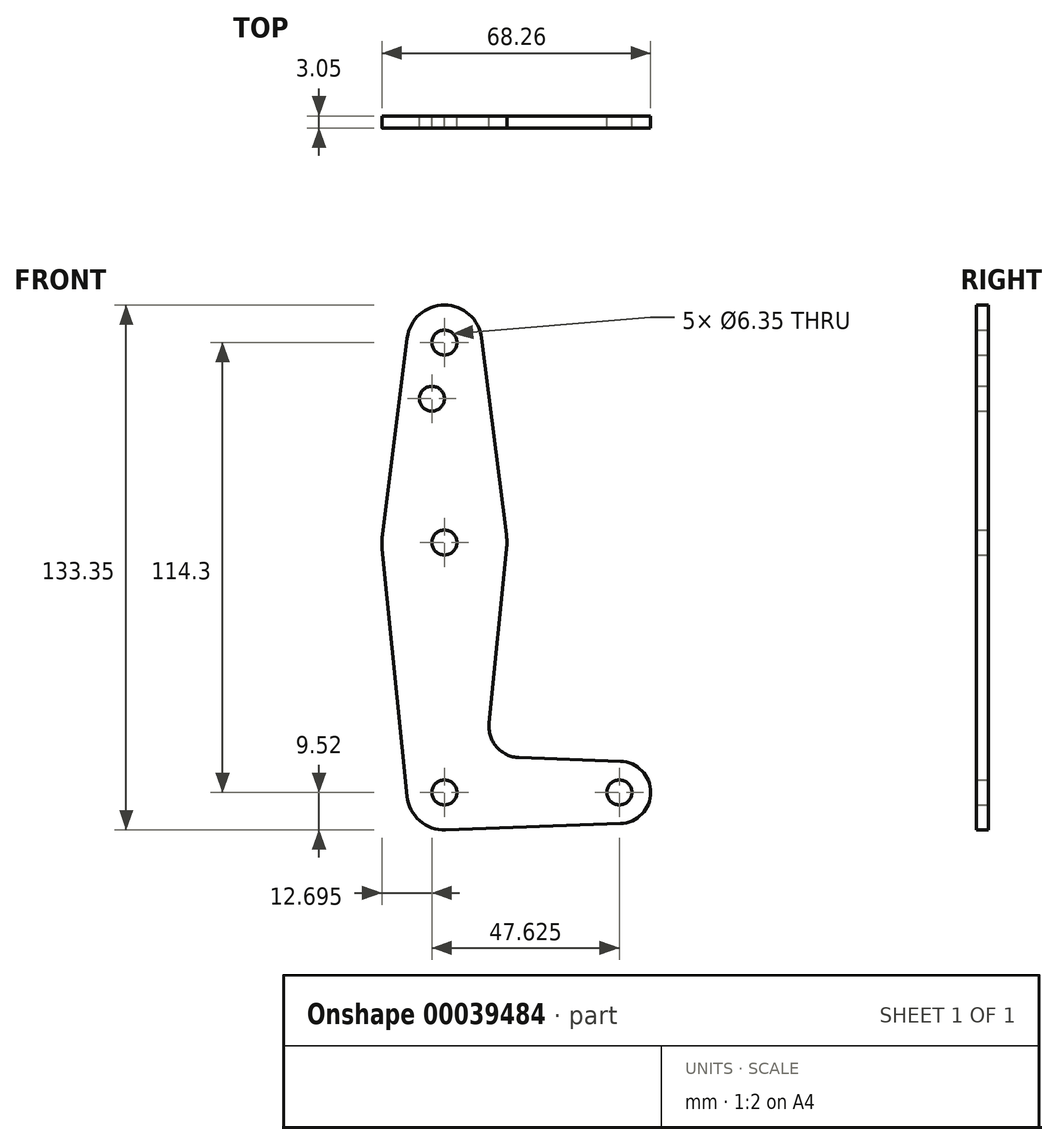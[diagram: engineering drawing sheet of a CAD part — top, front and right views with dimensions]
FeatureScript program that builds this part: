
annotation { "Feature Type Name" : "Feature", "Feature Type Description" : "" }
export const myFeature = defineFeature(function(context is Context, id is Id, definition is map)
    precondition{}
    {
        {
            var Q0;
            Q0=qCreatedBy(makeId("Front.planeOp"),FACE);
            var sketch = newSketch(context, id + "F0", { "sketchPlane" : qUnion([Q0])});
            skLineSegment(sketch, "E0", {"start": v(0, 0) * mm, "end": v(0, 114.3) * mm, "construction": true});
            skLineSegment(sketch, "E1", {"start": v(0, 0) * mm, "end": v(44.45, 0) * mm, "construction": true});
            skCircle(sketch, "E2", {"center": v(0, 114.3) * mm, "radius": 9.53 * mm});
            skCircle(sketch, "E3", {"center": v(0, 0) * mm, "radius": 9.53 * mm});
            skCircle(sketch, "E4", {"center": v(44.45, 0) * mm, "radius": 7.94 * mm});
            skCircle(sketch, "E5", {"center": v(0, 63.5) * mm, "radius": 15.88 * mm});
            skLineSegment(sketch, "E6", {"start": v(-9.45, 115.5) * mm, "end": v(-15.75, 65.48) * mm});
            skLineSegment(sketch, "E7", {"start": v(-9.48, -0.95) * mm, "end": v(-15.8, 61.91) * mm});
            skLineSegment(sketch, "E8", {"start": v(9.45, 115.5) * mm, "end": v(15.75, 65.48) * mm});
            skLineSegment(sketch, "E9", {"start": v(15.8, 61.91) * mm, "end": v(11.34, 17.6) * mm});
            skLineSegment(sketch, "E10", {"start": v(0.34, -9.52) * mm, "end": v(44.73, -7.93) * mm});
            skLineSegment(sketch, "E11", {"start": v(18.97, 8.85) * mm, "end": v(44.73, 7.93) * mm});
            skCircle(sketch, "E12", {"center": v(0, 114.3) * mm, "radius": 3.18 * mm});
            skCircle(sketch, "E13", {"center": v(-3.18, 100.03) * mm, "radius": 3.18 * mm});
            skCircle(sketch, "E14", {"center": v(0, 63.5) * mm, "radius": 3.18 * mm});
            skCircle(sketch, "E15", {"center": v(0, 0) * mm, "radius": 3.18 * mm});
            skCircle(sketch, "E16", {"center": v(44.45, 0) * mm, "radius": 3.18 * mm});
            skArc(sketch, "E17.filletArc", {"start": v(11.34, 17.6) * mm, "mid": v(13.26, 11.57) * mm, "end": v(18.97, 8.85) * mm});
            skSolve(sketch);
        }
        {
            var Q0;
            Q0 = qSketchRegion(id + "F0", true);
            extrude(context, id + "F1", {"entities" : qUnion([Q0]), "depth" : 3.05 * mm});
        }
    });
